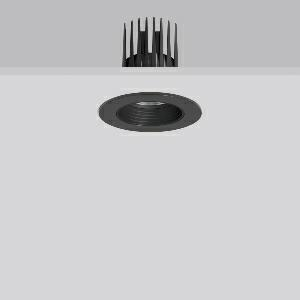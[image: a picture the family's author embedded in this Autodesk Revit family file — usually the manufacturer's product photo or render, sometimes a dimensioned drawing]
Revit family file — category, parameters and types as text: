
# Revit family: heledon_mini_e_901755_003_cd7d
name_source: partatom
category: Lighting Fixtures
units: mm (PartAtom-declared; Revit-internal decimal feet)

## family parameters
Cut with Voids When Loaded = No
Host = Face
Light Source = No
Part Type = Normal
Room Calculation Point = No
Round Connector Dimension = Use Diameter
Shared = No

## types (1)
- HELEDON mini E (1 x LED Modul 930, 2750 lm, 3000)
    Apparent Load = 29 VA
    Approval mark = CE
    CIE Flux Codes = 95 100 100 100 100
    Color Rendering = 90
    Color Temperature = 3000
    Default Elevation = 1800 mm
    Description = Series: HELEDON mini
Round recessed downlight. Housing: die-cast aluminium, powder-coated. Black plastic ring and recessed LED to prevent glare from the side. Optical assembly with lens made of plastic (polycarbonate) for the best homogeneous light distribution - can be changed without tools. Best colour rendering index Ra>90. Suitable for Recessed ceiling mounting. Installation without tools thanks to spring fastening system. Including separate LED converter with connecting cable 600 mm.High quality converter without flickering and stroboscopic effect. Through-wiring box (5 pole) available as accessory. The following accessories can be mounted without use of tools: interchangeable lenses, decorative glasses, honeycomb louvre, clear and frosted diffusers, white interchangeable plastic ring. 
Colour: deep black, matt (RAL 9005)
Diameter: 124 mm
Height: 3 mm
Cut-out diameter: 114 mm
Recess height: 170 mm
Luminaire: recess height: 120 mm
Lamp: LED
Socket: without socket
Colour temperature: 3000K
Colour rendering index (CRI): 92
System power: 29 W
Rated luminous flux: 2750 lm
Luminous efficiency: 95 lm/W
Control gear: Regulated power supply
Protection class: II
Type of protection: IP 20
    Height = 0 mm  [stored 0 ft]
    Lamp = 1 x LED Modul 930
    Lamp Light Flux = 2750 lm
    Lamp count = 1
    Length = 124 mm  [stored 0.406824 ft]
    Lifetime = 50000 h
    Luminous efficacy = 95 lm/W
    Manufacturer = RZB
    ModVariant = No
    Model = 901755.003
    Mounting Place = Ceiling
    Mounting Type = Recessed
    Number of Poles = 1
    OnlyDefault = Yes
    Power Factor = 1
    Product Name = HELEDON mini E
    Product group = Recessed downlights
    ProductGroupID = 402
    Protection Class = Protection class II
    Protection Degree = IP 20
    RLX_Detail_Level = 1
    RLX_Emergency_Light_Flux = 0 lm
    RLX_Emergency_Type = 0
    RLX_Emergency_Type_DB = No
    RlxData = <blob elided: 132489 chars, md5=fbb46863>
    Socket = socket
    Standby Power = 0 W
    System Light Flux = 2750 lm
    System Power = 29 W
    Type Comments = Product without accessories
    Type Image = 901656.003.jpg
    URL = http://relux.com
    VarID = ---
    Voltage = 230 V
    Voltage Range = 220-240 V
    Weight = 0.00 kg
    Width = 0 mm  [stored 0 ft]

note: [stored X ft] marks values corroborated as IEEE doubles in the binary element streams (Revit-internal decimal feet)

## geometry (parser evidence)
native form markers: Blend x4, Sweep x11
no freeform markers — native parametric forms only
